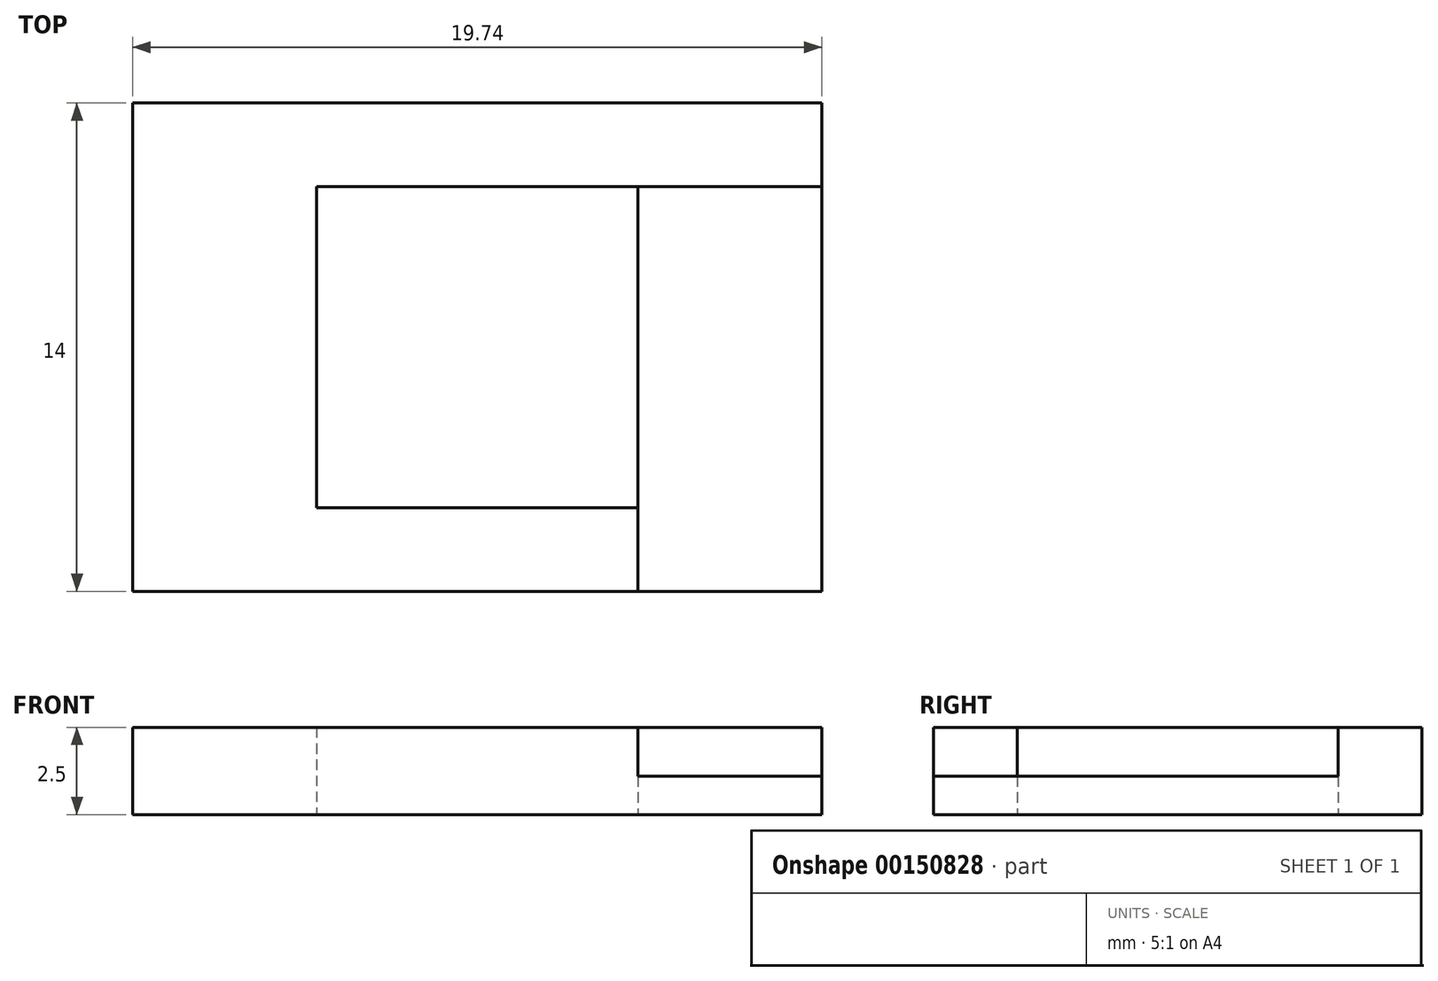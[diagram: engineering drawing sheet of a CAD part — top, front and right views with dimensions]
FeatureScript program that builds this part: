
annotation { "Feature Type Name" : "Feature", "Feature Type Description" : "" }
export const myFeature = defineFeature(function(context is Context, id is Id, definition is map)
    precondition{}
    {
        {
            var Q0;
            Q0=qCreatedBy(makeId("Top.planeOp"),FACE);
            var sketch = newSketch(context, id + "F0", { "sketchPlane" : qUnion([Q0])});
            skLineSegment(sketch, "E0", {"start": v(-7, 0) * mm, "end": v(7, 0) * mm, "construction": true});
            skLineSegment(sketch, "E1", {"start": v(0, 7) * mm, "end": v(0, -7) * mm, "construction": true});
            skLineSegment(sketch, "E2.bottom", {"start": v(4.6, 4.6) * mm, "end": v(-4.6, 4.6) * mm});
            skLineSegment(sketch, "E2.top", {"start": v(4.6, -4.6) * mm, "end": v(-4.6, -4.6) * mm});
            skLineSegment(sketch, "E2.left", {"start": v(4.6, 4.6) * mm, "end": v(4.6, -4.6) * mm});
            skLineSegment(sketch, "E2.right", {"start": v(-4.6, 4.6) * mm, "end": v(-4.6, -4.6) * mm});
            skPoint(sketch, "E2.middle", {"position": v(0, 0) * mm});
            skLineSegment(sketch, "E3.bottom", {"start": v(9.87, 7) * mm, "end": v(-9.87, 7) * mm});
            skLineSegment(sketch, "E3.top", {"start": v(9.87, -7) * mm, "end": v(-9.87, -7) * mm});
            skLineSegment(sketch, "E3.left", {"start": v(9.87, 7) * mm, "end": v(9.87, -7) * mm});
            skLineSegment(sketch, "E3.right", {"start": v(-9.87, 7) * mm, "end": v(-9.87, -7) * mm});
            skSolve(sketch);
        }
        {
            var Q0;
            Q0 = qSketchRegion(id + "F0", true);
            extrude(context, id + "F1", {"entities" : qUnion([Q0]), "depth" : 2.5 * mm});
        }
        {
            var Q0;
            Q0=makeQuery(id+"F1.opExtrude","CAP_FACE",FACE,{"disambiguationData":[OSD([sQuery(id+"F0.wireOp",EDGE,"E2.bottom"),sQuery(id+"F0.wireOp",EDGE,"E2.top"),sQuery(id+"F0.wireOp",EDGE,"E2.left"),sQuery(id+"F0.wireOp",EDGE,"E2.right"),sQuery(id+"F0.wireOp",EDGE,"Huugc7ue-pTXp-7fMj-MjGi-NxYififTvSa8")])],"isStart":false});
            var sketch = newSketch(context, id + "F2", { "sketchPlane" : qUnion([Q0])});
            skLineSegment(sketch, "E4.bottom", {"start": v(4.6, 4.6) * mm, "end": v(14.6, 4.6) * mm});
            skLineSegment(sketch, "E4.top", {"start": v(4.6, -15.4) * mm, "end": v(14.6, -15.4) * mm});
            skLineSegment(sketch, "E4.left", {"start": v(4.6, 4.6) * mm, "end": v(4.6, -15.4) * mm});
            skLineSegment(sketch, "E4.right", {"start": v(14.6, 4.6) * mm, "end": v(14.6, -15.4) * mm});
            skPoint(sketch, "E5.endSnap0", {"position": v(4.6, 0) * mm});
            skLineSegment(sketch, "E6", {"start": v(0, 0) * mm, "end": v(14.6, 0) * mm, "construction": true});
            skSolve(sketch);
        }
        {
            var Q0;
            Q0 = qSketchRegion(id + "F2", true);
            extrude(context, id + "F3", {"entities" : qUnion([Q0]), "operationType" : NewBodyOperationType.REMOVE, "oppositeDirection" : true, "depth" : 1.4 * mm});
        }
    });
